# Revit family: Worksurface-Teknion-HNBWRN_Navigate_Rectangular-R2016
name_source: partatom
category: Furniture
revit_build: Autodesk Revit Architecture 2016 (Build: 20190507_1515(x64)
units: mm (PartAtom-declared; Revit-internal decimal feet)

## family parameters
Always vertical = Yes
Cut with Voids When Loaded = No
OmniClass Number = 23.40.20.00
OmniClass Title = General Furniture and Specialties
Room Calculation Point = No
Shared = Yes
Work Plane-Based = No

## types (2) — shared parameters
Assembly Code = E2020200
Manufacturer = Teknion
Manufacturer Fax = 416.661.4586
Part Number = HNBWRN
Product Documentation Link = https://www.teknion.com
Product Line = Navigate Height-Adjustable Bench
Product Page URL = https://www.teknion.com
Series = Navigate Height-Adjustable Bench
Sustainability Data = https://www.teknion.com
URL = www.teknion.com
Unit Weight URL = http://www.teknion.com
Warranty = http://www.teknion.com

## per-type parameters (varying)
| type | Description | Model | Round Corner Profile Cut Hole Depth |
| Rounded (Leverage) Corner Profile | Navigate Rectangular Worksurface, Rounded (Leverage) Corner Profile | HNBWRN____1 | 7 " |
| Square Corner Profile | Navigate Rectangular Worksurface, Square Corner Profile | HNBWRN____2 | 3.25 " |

type visibility flags: 2 boolean params named "<type name>" — each type sets only its own to Yes (folded from table)

## geometry (parser evidence)
native form markers: Sweep x3
no freeform markers — native parametric forms only
